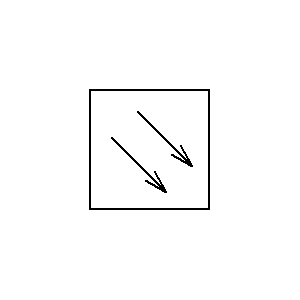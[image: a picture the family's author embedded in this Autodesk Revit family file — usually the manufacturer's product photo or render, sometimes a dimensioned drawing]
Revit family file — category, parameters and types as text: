
# Revit family: Gira_233602
name_source: partatom
category: Electrical Fixtures
revit_build: Autodesk Revit 2017 (Build: 20160225_1515(x64)
units: mm (PartAtom-declared; Revit-internal decimal feet)

## family parameters
Cut with Voids When Loaded = No
Host = Face
Maintain Annotation Orientation = No
Part Type = Normal
Room Calculation Point = No
Round Connector Dimension = Use Diameter
Shared = No

## types (1)
- SAD Basic Q Smoke alarm device p.white
    Available = No
    BIM (1) = https://media.stage.bim.site
    Backup battery included = None
    Cable entry = Bottom side
    Category = Fire detector
    Colour = White
    Current supply primary = Battery/accumulator
    Data sheet (1) = https://katalog.gira.de
    Default Elevation = 1219 mm
    Degree of protection (IP) = IP42
    Description = SAD Basic Q SAD PW,Smoke alarm device Basic Q,,pure white glossy,Increased quality criteria and technical advancements in smoke alarm devices are indicated on the market with the new Q test mark. The new Q-Label is an autonomous, manufacturer-independent quality mark for high-quality smoke alarm devices which undergo special testing for long-term use. The latest generation of Gira smoke alarm devices fulfil the criteria of the new Q-Label quality mark. The smoke alarm devices operate based on the photoelectric scattered light principle without radioactive particles. The smoke alarm devices detect smoke accumulation early and emit a warning signal before the concentration of smoke can become hazardous to people. Alerting occurs via a loud pulsing alarm tone and a flashing LED.,,Features:,- Use in private residential units or similarly inhabited areas only in accordance with DIN 14676.,Q-Label:,- Tested durability and reduction of deceptive alarms.,- Increased stability, e.g. against external factors.,- Permanently installed battery with a service life of up to 10 years.,- Design A as per DIN EN 14604.,- KRIWAN approval.,- Integrated function button for function test.,- Fault indication.,- Weak battery indication.
    Diameter = 0.125
    Explosion-tested version = No
    GTIN = 4010337013525
    HAN = 114502
    Height = 0.0385
    HeinzeBIM = https://bimportal.heinze.de
    Loudness = 85
    Manufacturer = Gira
    Manufacturer URL = https://www.gira.de
    Mounting method = Surface mounting
    Name = SAD Basic Q Smoke alarm device p.white
    Networkable via cable = No
    Networkable via radio optional = No
    Operating principle = Optic
    Smoke switcher = No
    Standalone = Yes
    Standard networkable via radio = No
    Suitable for duct mounting = No
    Supply voltage = 9 - 9
    Type of test-/pause button = Test button
    URL = http://katalog.gira.de
    VdS accepted = No
    Voltage type of supply voltage = Ac
    With backup battery = No
    With orientation lighting = No
    With socket = Yes
    With voltage indication = No

## geometry (parser evidence)
native form markers: Sweep x3
no freeform markers — native parametric forms only
